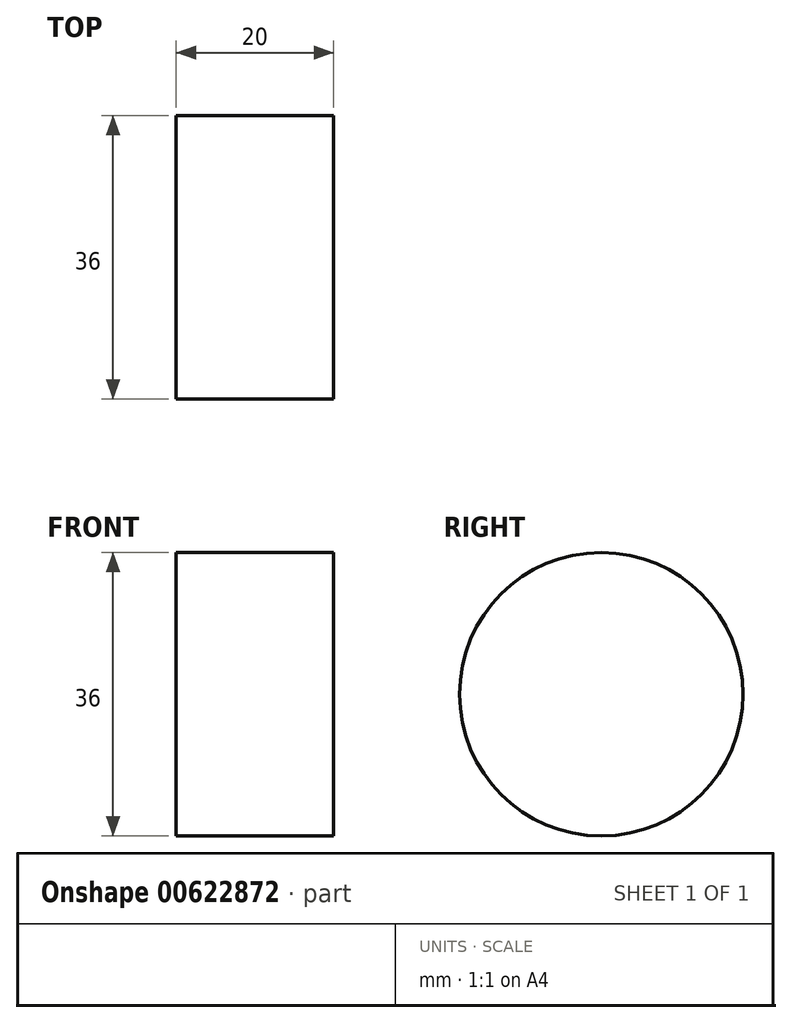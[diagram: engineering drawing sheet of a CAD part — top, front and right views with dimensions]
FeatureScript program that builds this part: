
annotation { "Feature Type Name" : "Feature", "Feature Type Description" : "" }
export const myFeature = defineFeature(function(context is Context, id is Id, definition is map)
    precondition{}
    {
        {
            var Q0;
            Q0=qCreatedBy(makeId("Right.planeOp"),FACE);
            var sketch = newSketch(context, id + "F0", { "sketchPlane" : qUnion([Q0])});
            skCircle(sketch, "E0", {"center": v(-24.8, 29.73) * mm, "radius": 18 * mm});
            skLineSegment(sketch, "E1", {"start": v(-42.8, 29.73) * mm, "end": v(-49.8, 29.73) * mm});
            skLineSegment(sketch, "E2", {"start": v(-51.8, 27.73) * mm, "end": v(-51.8, 19.73) * mm});
            skLineSegment(sketch, "E3", {"start": v(-51.8, 19.73) * mm, "end": v(-41.8, 19.73) * mm});
            skLineSegment(sketch, "E4", {"start": v(-41.8, 19.73) * mm, "end": v(-41.8, 15.73) * mm});
            skLineSegment(sketch, "E5", {"start": v(-24.84, 6.25) * mm, "end": v(-13.84, 6.25) * mm});
            skLineSegment(sketch, "E6", {"start": v(-13.84, 6.25) * mm, "end": v(-32.84, 6.25) * mm});
            skLineSegment(sketch, "E7", {"start": v(-32.84, 6.25) * mm, "end": v(-41.8, 15.73) * mm});
            skLineSegment(sketch, "E8", {"start": v(-13.84, 6.25) * mm, "end": v(-13.84, 12.25) * mm});
            skLineSegment(sketch, "E9", {"start": v(-13.84, 12.25) * mm, "end": v(-3.84, 12.25) * mm});
            skLineSegment(sketch, "E10", {"start": v(-9.87, 39.77) * mm, "end": v(1.9, 22.28) * mm});
            skArc(sketch, "E11", {"start": v(-3.84, 12.25) * mm, "mid": v(1.94, 15.6) * mm, "end": v(1.9, 22.28) * mm});
            skLineSegment(sketch, "E12", {"start": v(-13.84, 12.25) * mm, "end": v(-5.95, 3.25) * mm});
            skPoint(sketch, "E13.endSnap0", {"position": v(-3.99, 31.03) * mm});
            skCircle(sketch, "E14", {"center": v(39.16, 14.73) * mm, "radius": 11 * mm});
            skLineSegment(sketch, "E15", {"start": v(-5.95, 3.25) * mm, "end": v(39.16, 3.73) * mm});
            skLineSegment(sketch, "E16", {"start": v(39.16, 25.73) * mm, "end": v(-0.42, 25.73) * mm});
            skLineSegment(sketch, "E17", {"start": v(39.16, 25.73) * mm, "end": v(10.46, 25.73) * mm});
            skLineSegment(sketch, "E18", {"start": v(10.46, 25.73) * mm, "end": v(10.46, 32.02) * mm});
            skLineSegment(sketch, "E19", {"start": v(12.46, 34.02) * mm, "end": v(29.63, 34.02) * mm});
            skLineSegment(sketch, "E20", {"start": v(31.75, 33.14) * mm, "end": v(39.16, 25.73) * mm});
            skPoint(sketch, "E21.visualSharp", {"position": v(-51.8, 29.73) * mm});
            skArc(sketch, "E21.filletArc", {"start": v(-49.8, 29.73) * mm, "mid": v(-51.22, 29.14) * mm, "end": v(-51.8, 27.73) * mm});
            skPoint(sketch, "E22.visualSharp", {"position": v(10.46, 34.02) * mm});
            skArc(sketch, "E22.filletArc", {"start": v(12.46, 34.02) * mm, "mid": v(11.04, 33.43) * mm, "end": v(10.46, 32.02) * mm});
            skPoint(sketch, "E23.visualSharp", {"position": v(30.87, 34.02) * mm});
            skArc(sketch, "E23.filletArc", {"start": v(31.75, 33.14) * mm, "mid": v(30.78, 33.8) * mm, "end": v(29.63, 34.02) * mm});
            skFitSpline(sketch, "E24", {"points": [v(-15.22, 6.25) * mm, v(-13.84, 7.76) * mm], "startDerivative": vector(2.92, 0) * mm, "endDerivative": vector(0, 2.49) * mm});
            skSolve(sketch);
        }
        {
            var Q0;
            {var subQ0=sQuery(id+"F0.wireOp",EDGE,"E0");var subQ1=makeQuery(id+"F0.imprint","INTERSECT",VERTEX,{"derivedFrom":[subQ0,sQuery(id+"F0.wireOp",EDGE,"E1")]});Q0=makeQuery(id+"F0.imprint","IMPRINT",FACE,{"disambiguationData":[TD([[makeQuery(id+"F0.imprint","IMPRINT",EDGE,{"disambiguationData":[TD([[subQ1,1.0]])],"derivedFrom":subQ0}),1.0]])]});}
            extrude(context, id + "F1", {"entities" : qUnion([Q0]), "depth" : 20 * mm, "offsetDistance" : 25 * mm});
        }
    });
